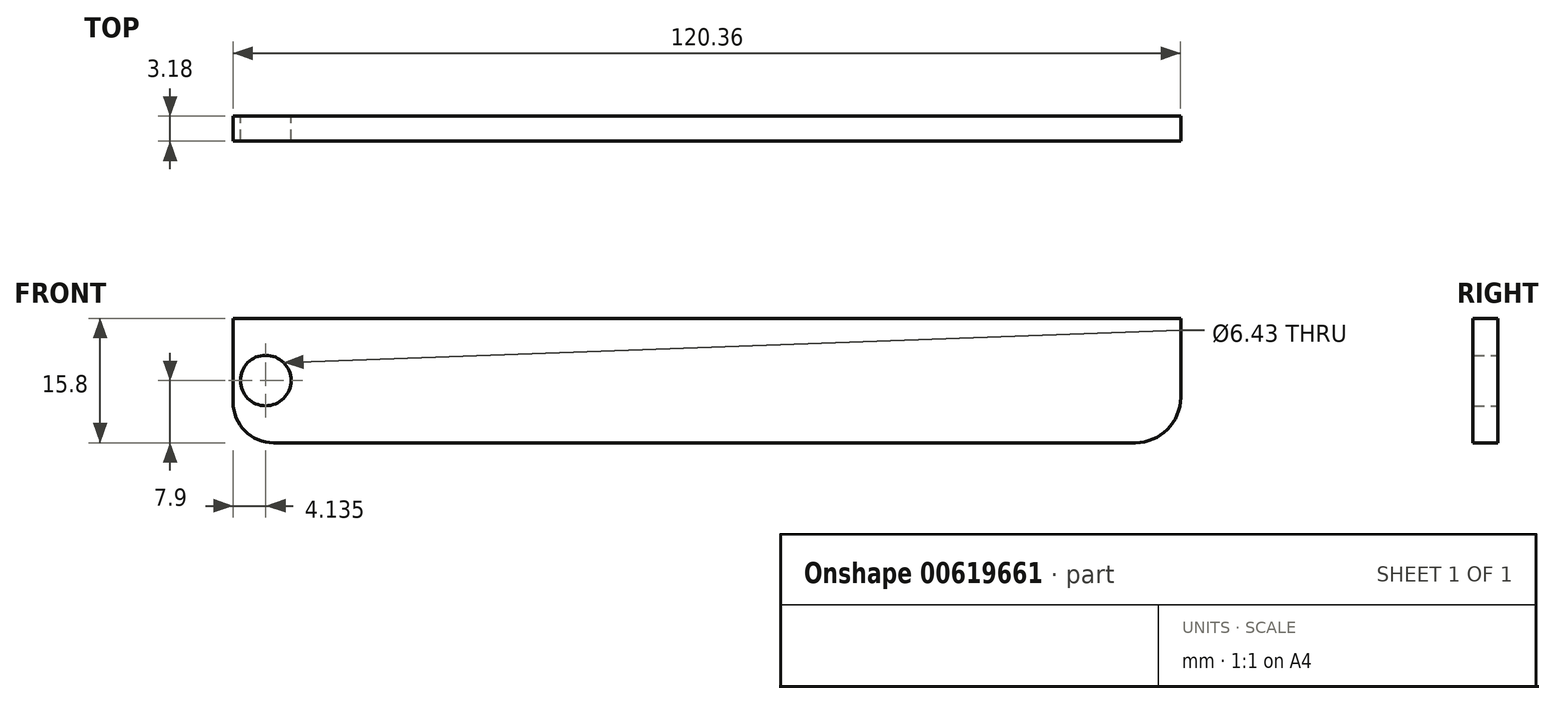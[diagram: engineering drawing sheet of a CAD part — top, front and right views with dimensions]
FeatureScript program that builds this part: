
annotation { "Feature Type Name" : "Feature", "Feature Type Description" : "" }
export const myFeature = defineFeature(function(context is Context, id is Id, definition is map)
    precondition{}
    {
        {
            var Q0;
            Q0=qCreatedBy(makeId("Front.planeOp"),FACE);
            var sketch = newSketch(context, id + "F0", { "sketchPlane" : qUnion([Q0])});
            skLineSegment(sketch, "E0.bottom", {"start": v(-60.18, 7.9) * mm, "end": v(60.18, 7.9) * mm});
            skLineSegment(sketch, "E0.top", {"start": v(-55.05, -7.9) * mm, "end": v(54.42, -7.9) * mm});
            skLineSegment(sketch, "E0.left", {"start": v(-60.18, 7.9) * mm, "end": v(-60.18, -2.76) * mm});
            skLineSegment(sketch, "E0.right", {"start": v(60.18, 7.9) * mm, "end": v(60.18, -2.13) * mm});
            skPoint(sketch, "E0.middle", {"position": v(0, 0) * mm});
            skLineSegment(sketch, "E1.bottom", {"start": v(-60.18, 7.9) * mm, "end": v(-46.83, 7.9) * mm});
            skLineSegment(sketch, "E1.top", {"start": v(-57.24, 29.75) * mm, "end": v(-46.83, 29.75) * mm});
            skLineSegment(sketch, "E1.left", {"start": v(-60.18, 7.9) * mm, "end": v(-60.18, 26.8) * mm});
            skLineSegment(sketch, "E1.right", {"start": v(-46.83, 7.9) * mm, "end": v(-46.83, 29.75) * mm});
            skLineSegment(sketch, "E2.bottom", {"start": v(60.18, 7.9) * mm, "end": v(46.02, 7.9) * mm});
            skLineSegment(sketch, "E2.top", {"start": v(55.05, 29.75) * mm, "end": v(51.24, 29.75) * mm});
            skLineSegment(sketch, "E2.left", {"start": v(60.18, 7.9) * mm, "end": v(60.18, 24.6) * mm});
            skLineSegment(sketch, "E2.right", {"start": v(46.02, 7.9) * mm, "end": v(46.02, 24.53) * mm});
            skPoint(sketch, "E3.visualSharp", {"position": v(-60.18, 29.75) * mm});
            skArc(sketch, "E3.filletArc", {"start": v(-57.24, 29.75) * mm, "mid": v(-59.32, 28.88) * mm, "end": v(-60.18, 26.8) * mm});
            skPoint(sketch, "E4.visualSharp", {"position": v(60.18, 29.75) * mm});
            skArc(sketch, "E4.filletArc", {"start": v(60.18, 24.6) * mm, "mid": v(58.68, 28.24) * mm, "end": v(55.05, 29.75) * mm});
            skPoint(sketch, "E5.visualSharp", {"position": v(-60.18, -7.9) * mm});
            skArc(sketch, "E5.filletArc", {"start": v(-60.18, -2.76) * mm, "mid": v(-58.68, -6.4) * mm, "end": v(-55.05, -7.9) * mm});
            skPoint(sketch, "E6.visualSharp", {"position": v(60.18, -7.9) * mm});
            skArc(sketch, "E6.filletArc", {"start": v(54.42, -7.9) * mm, "mid": v(58.5, -6.21) * mm, "end": v(60.18, -2.13) * mm});
            skPoint(sketch, "E7.centerSnap0", {"position": v(-60.18, 17.35) * mm});
            skCircle(sketch, "E8", {"center": v(50.54, 17.37) * mm, "radius": 3.4 * mm});
            skPoint(sketch, "E8.centerSnap0", {"position": v(50.54, 29.75) * mm});
            skCircle(sketch, "E9", {"center": v(-56.05, 0) * mm, "radius": 3.21 * mm});
            skPoint(sketch, "E10.visualSharp", {"position": v(46.02, 29.75) * mm});
            skArc(sketch, "E10.filletArc", {"start": v(51.24, 29.75) * mm, "mid": v(47.55, 28.22) * mm, "end": v(46.02, 24.53) * mm});
            skPoint(sketch, "E7.center.orphan", {"position": v(-53.41, 17.35) * mm});
            skSolve(sketch);
        }
        {
            var Q0;
            Q0=makeQuery(id+"F0.imprint","IMPRINT",FACE,{"disambiguationData":[TD([[makeQuery(id+"F0.imprint","IMPRINT",EDGE,{"derivedFrom":sQuery(id+"F0.wireOp",EDGE,"E0.bottom")}),-1.0]])]});
            var Q1;
            Q1=makeQuery(id+"F0.imprint","IMPRINT",FACE,{"disambiguationData":[TD([[makeQuery(id+"F0.imprint","IMPRINT",EDGE,{"derivedFrom":sQuery(id+"F0.wireOp",EDGE,"E2.bottom")}),-1.0]])]});
            var Q2;
            Q2=makeQuery(id+"F0.imprint","IMPRINT",FACE,{"disambiguationData":[TD([[makeQuery(id+"F0.imprint","IMPRINT",EDGE,{"derivedFrom":sQuery(id+"F0.wireOp",EDGE,"E1.bottom")}),1.0]])]});
            extrude(context, id + "F1", {"entities" : qUnion([Q0, Q1, Q2]), "depth" : 3.17 * mm, "offsetDistance" : 25.4 * mm});
        }
    });
